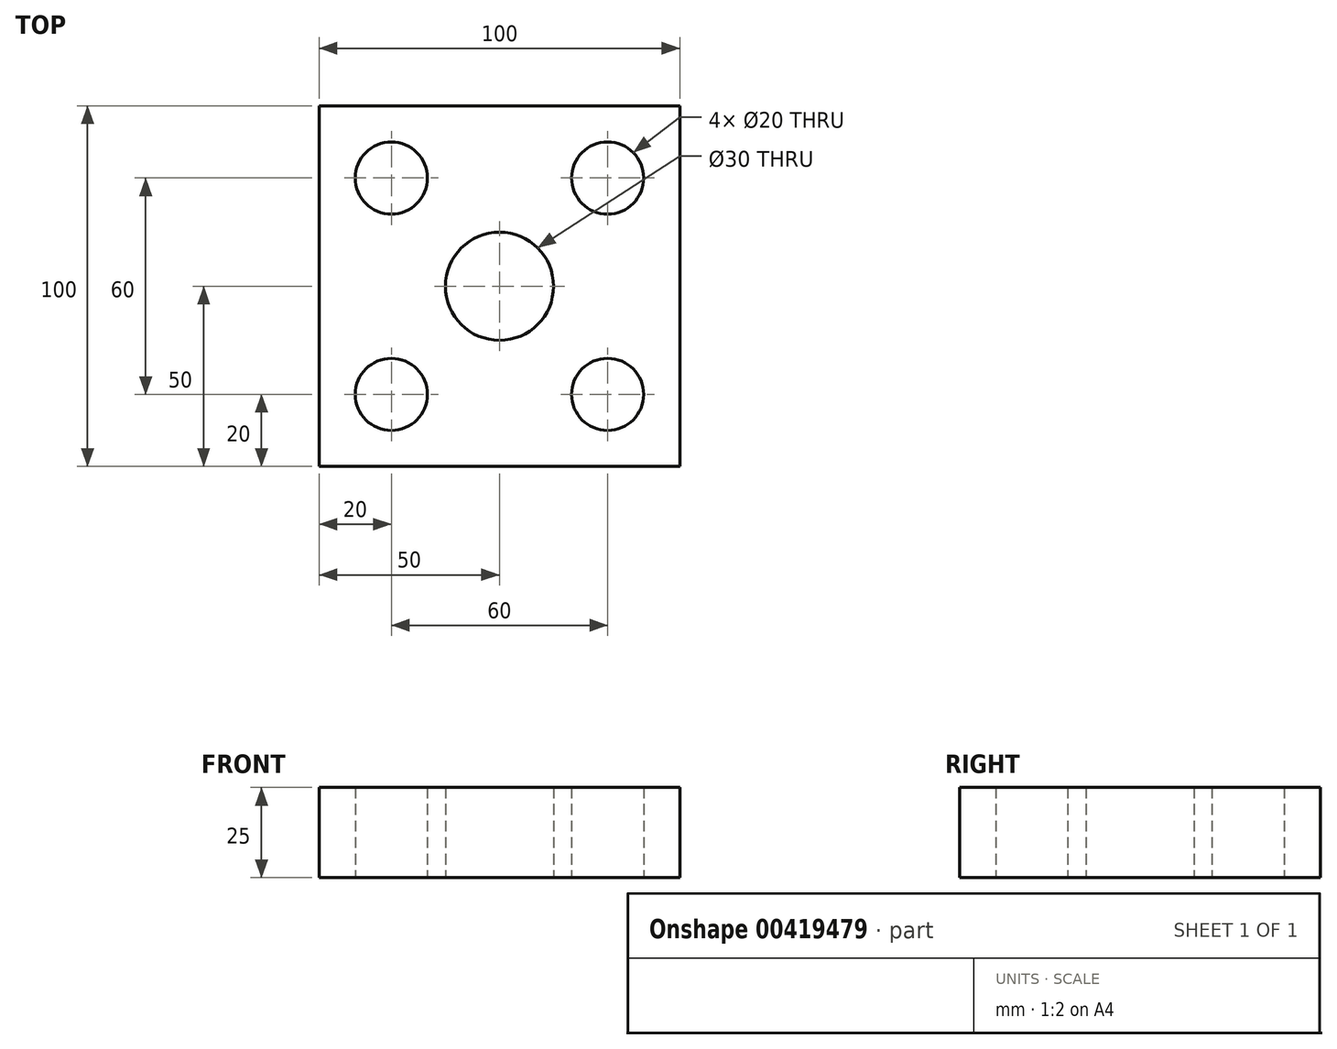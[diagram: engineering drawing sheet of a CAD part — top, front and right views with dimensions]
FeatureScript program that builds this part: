
annotation { "Feature Type Name" : "Feature", "Feature Type Description" : "" }
export const myFeature = defineFeature(function(context is Context, id is Id, definition is map)
    precondition{}
    {
        {
            var Q0;
            Q0=qCreatedBy(makeId("Top.planeOp"),FACE);
            var sketch = newSketch(context, id + "F0", { "sketchPlane" : qUnion([Q0])});
            skLineSegment(sketch, "E0.bottom", {"start": v(50, 50) * mm, "end": v(-50, 50) * mm});
            skLineSegment(sketch, "E0.top", {"start": v(50, -50) * mm, "end": v(-50, -50) * mm});
            skLineSegment(sketch, "E0.left", {"start": v(50, 50) * mm, "end": v(50, -50) * mm});
            skLineSegment(sketch, "E0.right", {"start": v(-50, 50) * mm, "end": v(-50, -50) * mm});
            skPoint(sketch, "E0.middle", {"position": v(0, 0) * mm});
            skCircle(sketch, "E1", {"center": v(0, 0) * mm, "radius": 15 * mm});
            skCircle(sketch, "E2", {"center": v(-30, 30) * mm, "radius": 10 * mm});
            skCircle(sketch, "E3", {"center": v(-30, -30) * mm, "radius": 10 * mm});
            skCircle(sketch, "E4", {"center": v(30, -30) * mm, "radius": 10 * mm});
            skCircle(sketch, "E5", {"center": v(30, 30) * mm, "radius": 10 * mm});
            skSolve(sketch);
        }
        {
            var Q0;
            Q0=qSketchRegion(id+"F0",true);
            extrude(context, id + "F1", {"entities" : qUnion([Q0]), "depth" : 25 * mm});
        }
    });
